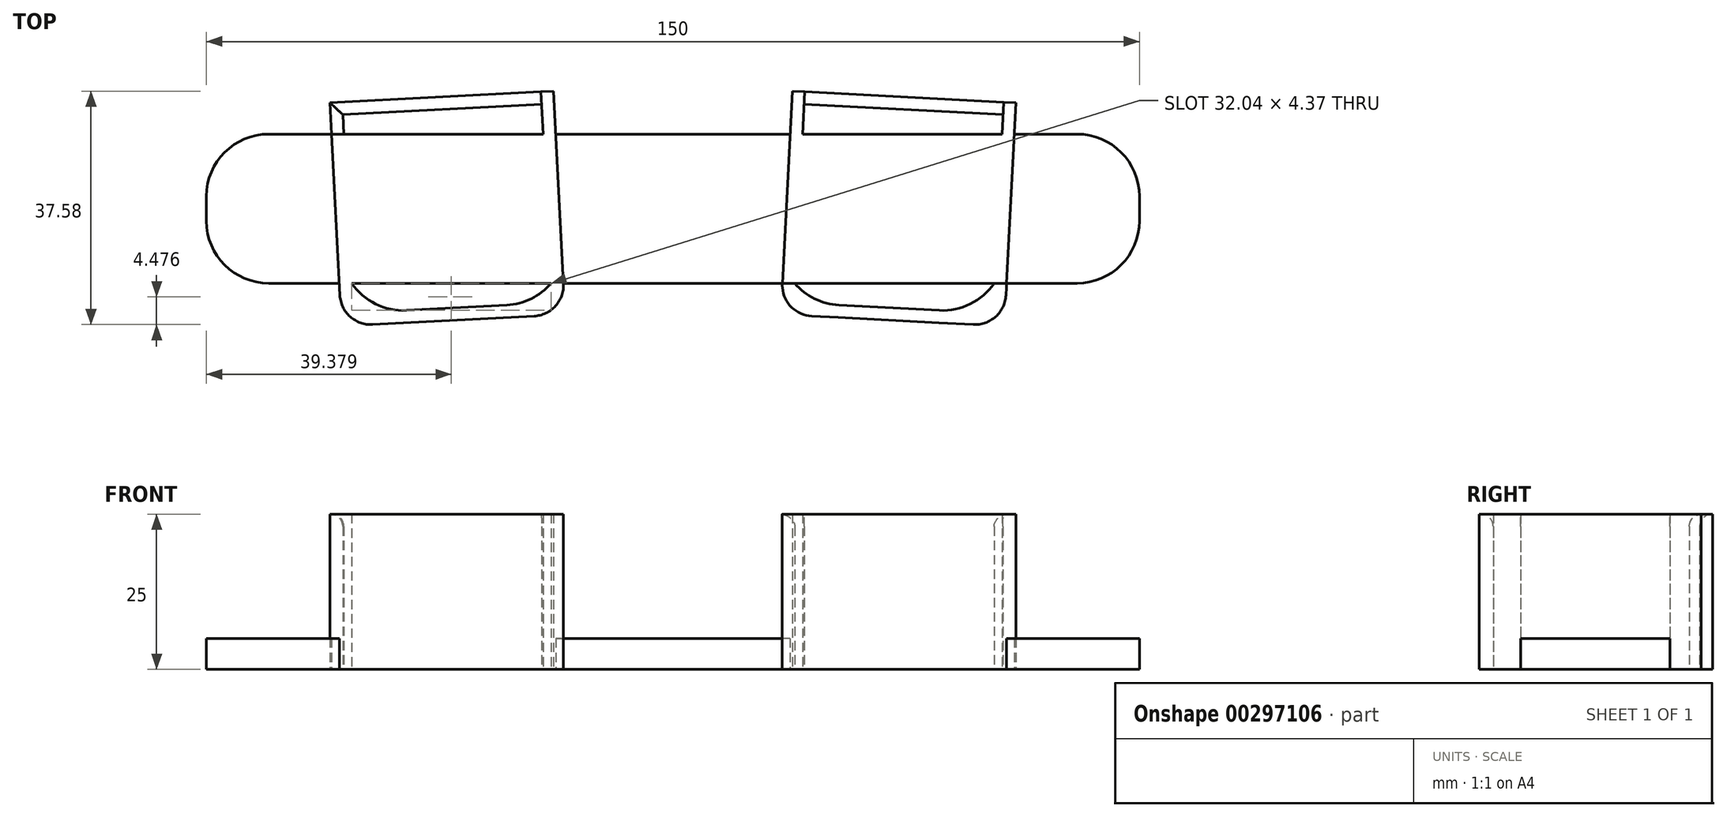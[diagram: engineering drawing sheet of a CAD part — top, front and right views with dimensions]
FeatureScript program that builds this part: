
annotation { "Feature Type Name" : "Feature", "Feature Type Description" : "" }
export const myFeature = defineFeature(function(context is Context, id is Id, definition is map)
    precondition{}
    {
        {
            var Q0;
            Q0=qCreatedBy(makeId("Top.planeOp"),FACE);
            var sketch = newSketch(context, id + "F0", { "sketchPlane" : qUnion([Q0])});
            skLineSegment(sketch, "E0", {"start": v(-36.25, 0) * mm, "end": v(36.25, 0) * mm, "construction": true});
            skLineSegment(sketch, "E1.bottom", {"start": v(-53.07, 15.14) * mm, "end": v(-21.1, 16.82) * mm});
            skLineSegment(sketch, "E1.top", {"start": v(-51.4, -16.82) * mm, "end": v(-19.43, -15.14) * mm});
            skLineSegment(sketch, "E1.left", {"start": v(-53.07, 15.14) * mm, "end": v(-51.4, -16.82) * mm});
            skLineSegment(sketch, "E1.right", {"start": v(-21.1, 16.82) * mm, "end": v(-19.43, -15.14) * mm});
            skPoint(sketch, "E1.middle", {"position": v(-36.25, 0) * mm});
            skLineSegment(sketch, "E2.1", {"start": v(-49.5, 12) * mm, "end": v(-25.5, 12) * mm});
            skLineSegment(sketch, "E2.3", {"start": v(-49.5, -12) * mm, "end": v(-25.5, -12) * mm});
            skLineSegment(sketch, "E3.bottom", {"start": v(0, 12) * mm, "end": v(-75, 12) * mm});
            skLineSegment(sketch, "E3.top", {"start": v(0, -12) * mm, "end": v(-75, -12) * mm});
            skLineSegment(sketch, "E3.left", {"start": v(0, 12) * mm, "end": v(0, -12) * mm});
            skLineSegment(sketch, "E3.right", {"start": v(-75, 12) * mm, "end": v(-75, -12) * mm});
            skLineSegment(sketch, "E4.0", {"start": v(-55.17, 17.03) * mm, "end": v(-53.28, -18.92) * mm});
            skLineSegment(sketch, "E4.1", {"start": v(-55.17, 17.03) * mm, "end": v(-19.22, 18.92) * mm});
            skLineSegment(sketch, "E4.2", {"start": v(-19.22, 18.92) * mm, "end": v(-17.33, -17.03) * mm});
            skLineSegment(sketch, "E4.3", {"start": v(-53.28, -18.92) * mm, "end": v(-17.33, -17.03) * mm});
            skLineSegment(sketch, "E5", {"start": v(-21.1, 16.82) * mm, "end": v(-51.4, -16.82) * mm});
            skSolve(sketch);
        }
        {
            var Q0;
            {var subQ6=sQuery(id+"F0.wireOp",EDGE,"E1.bottom");Q0=makeQuery(id+"F0.imprint","IMPRINT",FACE,{"disambiguationData":[TD([[makeQuery(id+"F0.imprint","IMPRINT",EDGE,{"derivedFrom":subQ6}),1.0]])]});}
            var Q1;
            {var subQ0=sQuery(id+"F0.wireOp",EDGE,"E3.bottom");var subQ1=sQuery(id+"F0.wireOp",EDGE,"E1.left");var subQ2=makeQuery(id+"F0.imprint","INTERSECT",VERTEX,{"derivedFrom":[subQ1,subQ0]});Q1=makeQuery(id+"F0.imprint","IMPRINT",FACE,{"disambiguationData":[TD([[makeQuery(id+"F0.imprint","IMPRINT",EDGE,{"disambiguationData":[TD([[subQ2,-1.0]])],"derivedFrom":subQ1}),-1.0]])]});}
            var Q2;
            {var subQ0=sQuery(id+"F0.wireOp",EDGE,"E3.bottom");var subQ1=sQuery(id+"F0.wireOp",EDGE,"E1.right");var subQ2=makeQuery(id+"F0.imprint","INTERSECT",VERTEX,{"derivedFrom":[subQ1,subQ0]});Q2=makeQuery(id+"F0.imprint","IMPRINT",FACE,{"disambiguationData":[TD([[makeQuery(id+"F0.imprint","IMPRINT",EDGE,{"disambiguationData":[TD([[subQ2,-1.0]])],"derivedFrom":subQ1}),1.0]])]});}
            var Q3;
            {var subQ5=sQuery(id+"F0.wireOp",EDGE,"E1.top");Q3=makeQuery(id+"F0.imprint","IMPRINT",FACE,{"disambiguationData":[TD([[makeQuery(id+"F0.imprint","IMPRINT",EDGE,{"derivedFrom":subQ5}),-1.0]])]});}
            var Q4;
            {var subQ4=sQuery(id+"F0.wireOp",EDGE,"E2.1");Q4=makeQuery(id+"F0.imprint","IMPRINT",FACE,{"disambiguationData":[TD([[makeQuery(id+"F0.imprint","IMPRINT",EDGE,{"derivedFrom":subQ4}),-1.0]])]});}
            var Q5;
            {var subQ4=sQuery(id+"F0.wireOp",EDGE,"E2.3");Q5=makeQuery(id+"F0.imprint","IMPRINT",FACE,{"disambiguationData":[TD([[makeQuery(id+"F0.imprint","IMPRINT",EDGE,{"derivedFrom":subQ4}),1.0]])]});}
            var Q6;
            {var subQ0=sQuery(id+"F0.wireOp",EDGE,"E4.2");var subQ1=sQuery(id+"F0.wireOp",EDGE,"E3.bottom");var subQ2=makeQuery(id+"F0.imprint","INTERSECT",VERTEX,{"derivedFrom":[subQ1,subQ0]});Q6=makeQuery(id+"F0.imprint","IMPRINT",FACE,{"disambiguationData":[TD([[makeQuery(id+"F0.imprint","IMPRINT",EDGE,{"disambiguationData":[TD([[subQ2,-1.0]])],"derivedFrom":subQ1}),-1.0]])]});}
            var Q7;
            {var subQ0=sQuery(id+"F0.wireOp",EDGE,"E4.3");var subQ1=sQuery(id+"F0.wireOp",EDGE,"E3.top");var subQ2=makeQuery(id+"F0.imprint","INTERSECT",VERTEX,{"derivedFrom":[subQ1,subQ0]});Q7=makeQuery(id+"F0.imprint","IMPRINT",FACE,{"disambiguationData":[TD([[makeQuery(id+"F0.imprint","IMPRINT",EDGE,{"disambiguationData":[TD([[subQ2,-1.0]])],"derivedFrom":subQ1}),1.0]])]});}
            extrude(context, id + "F1", {"entities" : qUnion([Q0, Q1, Q2, Q3, Q4, Q5, Q6, Q7]), "depth" : 25 * mm});
        }
        {
            var Q0;
            {var subQ5=sQuery(id+"F0.wireOp",EDGE,"E3.right");Q0=makeQuery(id+"F0.imprint","IMPRINT",FACE,{"disambiguationData":[TD([[makeQuery(id+"F0.imprint","IMPRINT",EDGE,{"derivedFrom":subQ5}),1.0]])]});}
            var Q1;
            {var subQ5=sQuery(id+"F0.wireOp",EDGE,"E3.left");Q1=makeQuery(id+"F0.imprint","IMPRINT",FACE,{"disambiguationData":[TD([[makeQuery(id+"F0.imprint","IMPRINT",EDGE,{"derivedFrom":subQ5}),-1.0]])]});}
            extrude(context, id + "F2", {"entities" : qUnion([Q0, Q1]), "operationType" : NewBodyOperationType.ADD, "depth" : 5 * mm});
        }
        {
            var Q0;
            Q0=makeQuery(id+"F2.opExtrude","SWEPT_EDGE",EDGE,{"disambiguationData":[OSD([sQuery(id+"F0.wireOp",EDGE,"E3.top"),sQuery(id+"F0.wireOp",EDGE,"E3.right")])]});
            var Q1;
            Q1=makeQuery(id+"F2.opExtrude","SWEPT_EDGE",EDGE,{"disambiguationData":[OSD([sQuery(id+"F0.wireOp",EDGE,"E3.bottom"),sQuery(id+"F0.wireOp",EDGE,"E3.right")])]});
            var Q2;
            Q2=makeQuery(id+"F1.opExtrude","SWEPT_EDGE",EDGE,{"disambiguationData":[OSD([sQuery(id+"F0.wireOp",EDGE,"E1.top"),sQuery(id+"F0.wireOp",EDGE,"E1.left"),sQuery(id+"F0.wireOp",EDGE,"E5")])]});
            var Q3;
            Q3=makeQuery(id+"F1.opExtrude","SWEPT_EDGE",EDGE,{"disambiguationData":[OSD([sQuery(id+"F0.wireOp",EDGE,"E1.top"),sQuery(id+"F0.wireOp",EDGE,"E1.right")])]});
            fillet(context, id + "F3", {"entities" : qUnion([Q0, Q1, Q2, Q3]), "radius" : 10 * mm, "tangentPropagation" : true, "allowEdgeOverflow" : false});
        }
        {
            var Q0;
            Q0=makeQuery(id+"F1.opExtrude","SWEPT_EDGE",EDGE,{"disambiguationData":[OSD([sQuery(id+"F0.wireOp",EDGE,"E4.0"),sQuery(id+"F0.wireOp",EDGE,"E4.3")])]});
            var Q1;
            Q1=makeQuery(id+"F1.opExtrude","SWEPT_EDGE",EDGE,{"disambiguationData":[OSD([sQuery(id+"F0.wireOp",EDGE,"E4.2"),sQuery(id+"F0.wireOp",EDGE,"E4.3")])]});
            fillet(context, id + "F4", {"entities" : qUnion([Q0, Q1]), "radius" : 5 * mm, "tangentPropagation" : true, "allowEdgeOverflow" : false});
        }
        {
            var Q0;
            Q0=makeQuery(id+"F1.opExtrude","SWEPT_BODY",BODY,{"disambiguationData":[OSD([sQuery(id+"F0.wireOp",EDGE,"E1.left"),sQuery(id+"F0.wireOp",EDGE,"E1.right"),sQuery(id+"F0.wireOp",EDGE,"E2.0"),sQuery(id+"F0.wireOp",EDGE,"E2.1"),sQuery(id+"F0.wireOp",EDGE,"E2.2"),sQuery(id+"F0.wireOp",EDGE,"E2.3"),sQuery(id+"F0.wireOp",EDGE,"E3.bottom"),sQuery(id+"F0.wireOp",EDGE,"E3.top")])]});
            var Q1;
            Q1=qCreatedBy(makeId("Right.planeOp"),FACE);
            mirror(context, id + "F5", {"operationType" : NewBodyOperationType.ADD, "entities" : qUnion([Q0]), "mirrorPlane" : qUnion([Q1])});
        }
        {
            var Q0;
            Q0=makeQuery(id+"F1.opExtrude","CAP_EDGE",EDGE,{"disambiguationData":[OSD([sQuery(id+"F0.wireOp",EDGE,"E1.left")])],"isStart":false});
            var Q1;
            Q1=makeQuery(id+"F1.opExtrude","CAP_EDGE",EDGE,{"disambiguationData":[OSD([sQuery(id+"F0.wireOp",EDGE,"E1.bottom")])],"isStart":false});
            var Q2;
            Q2=makeQuery(id+"F5.opPattern","COPY",EDGE,{"derivedFrom":makeQuery(id+"F1.opExtrude","CAP_EDGE",EDGE,{"disambiguationData":[OSD([sQuery(id+"F0.wireOp",EDGE,"E1.bottom")])],"isStart":false}),"instanceName":"1"});
            var Q3;
            {var subQ0=sQuery(id+"F0.wireOp",EDGE,"E1.left");var subQ1=sQuery(id+"F0.wireOp",EDGE,"E1.top");Q3=makeQuery(id+"F5.opPattern","COPY",EDGE,{"derivedFrom":makeQuery(id+"F3.opFillet","BLEND_EDGE",EDGE,{"blendedFrom":[makeQuery(id+"F1.opExtrude","SWEPT_EDGE",EDGE,{"disambiguationData":[OSD([subQ1,subQ0])]}),makeQuery(id+"F1.opExtrude","CAP_FACE",FACE,{"disambiguationData":[OSD([sQuery(id+"F0.wireOp",EDGE,"E1.bottom"),subQ1,subQ0,sQuery(id+"F0.wireOp",EDGE,"E1.right"),sQuery(id+"F0.wireOp",EDGE,"E2.0"),sQuery(id+"F0.wireOp",EDGE,"E2.2"),sQuery(id+"F0.wireOp",EDGE,"E3.bottom"),sQuery(id+"F0.wireOp",EDGE,"E3.top")])],"isStart":false})],"blendedInto":[makeQuery(id+"F1.opExtrude","CAP_FACE",FACE,{"disambiguationData":[OSD([sQuery(id+"F0.wireOp",EDGE,"E1.bottom"),subQ1,subQ0,sQuery(id+"F0.wireOp",EDGE,"E1.right"),sQuery(id+"F0.wireOp",EDGE,"E2.0"),sQuery(id+"F0.wireOp",EDGE,"E2.2"),sQuery(id+"F0.wireOp",EDGE,"E3.bottom"),sQuery(id+"F0.wireOp",EDGE,"E3.top")])],"isStart":false})]}),"instanceName":"1"});}
            fillet(context, id + "F6", {"entities" : qUnion([Q0, Q1, Q2, Q3]), "radius" : 2 * mm, "tangentPropagation" : true, "allowEdgeOverflow" : false});
        }
    });
